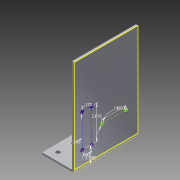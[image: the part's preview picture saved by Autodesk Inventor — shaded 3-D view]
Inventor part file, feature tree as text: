
AUTODESK INVENTOR PART (.ipt)
format: ipt  version: 2013 (Build 170138000, 138)  size: 122,368 bytes
history: native  units: in
note: dims shown in document units (in); Inventor stores cm internally (conversion verified against a paired STEP export)
features: sheet_metal_op x4, sketch x3, other x2
ambient origin geometry x8: Origin, YZ Plane, XZ Plane, XY Plane, X Axis, Y Axis, Z Axis, Center Point
bodies: Solid1 (feature_tree)
feature tree (9):
  sheet_metal_op  "Face1"
  sheet_metal_op  "Flange1"
  sketch  "Sketch3"  dims[d3=0.26in d4=1.0in d5=2.0in d6=0.5in d7=0.125in d8=1.0in d9=0.125in d10=0.0625in d11=0.25in d12=0.125in d13=6.0in d14=90.0deg d15=0.05in d16=0.5in d17=0.125in d18=0.125in d19=2.075in d21=0.6in d22=0.175in d23=1.0in d24=0.5in d25=1.5in d26=0.175in]
  sketch  "Sketch1"  dims[d0=4.0in]
  other  "Plate1"
  sketch  "Sketch2"  dims[d2=1.0in]
  other  "Plate2"
  sheet_metal_op  "Bend1"
  sheet_metal_op  "Corner1"
